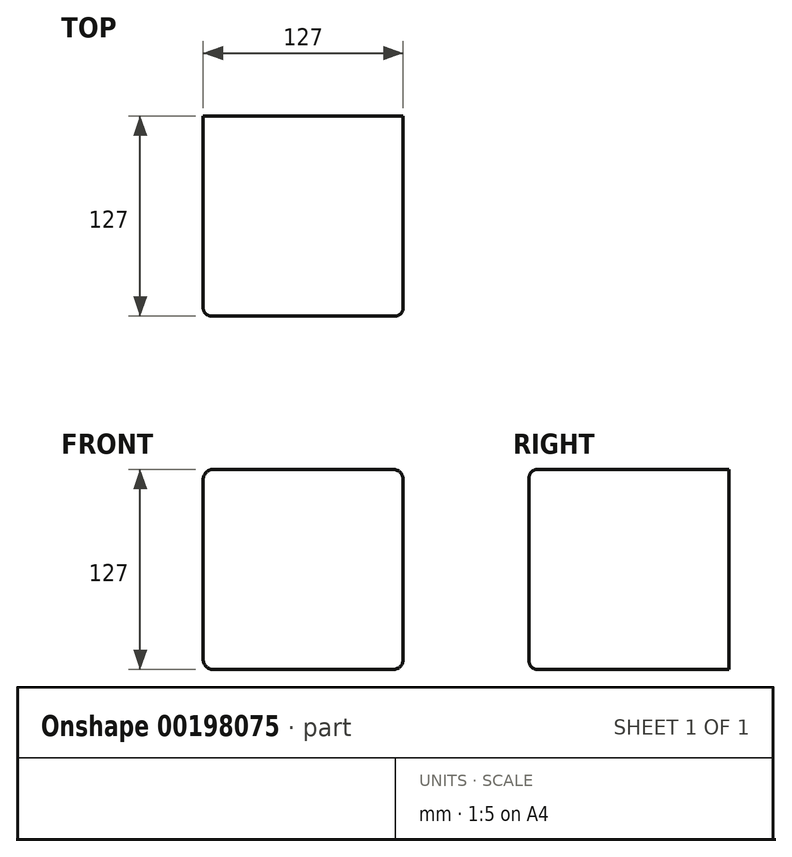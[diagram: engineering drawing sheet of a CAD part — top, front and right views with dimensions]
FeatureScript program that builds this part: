
annotation { "Feature Type Name" : "Feature", "Feature Type Description" : "" }
export const myFeature = defineFeature(function(context is Context, id is Id, definition is map)
    precondition{}
    {
        {
            var Q0;
            Q0=qCreatedBy(makeId("Front.planeOp"),FACE);
            var sketch = newSketch(context, id + "F0", { "sketchPlane" : qUnion([Q0])});
            skLineSegment(sketch, "E0.bottom", {"start": v(57.15, 63.5) * mm, "end": v(-57.15, 63.5) * mm});
            skLineSegment(sketch, "E0.top", {"start": v(57.15, -63.5) * mm, "end": v(-57.15, -63.5) * mm});
            skLineSegment(sketch, "E0.left", {"start": v(63.5, 57.15) * mm, "end": v(63.5, -57.15) * mm});
            skLineSegment(sketch, "E0.right", {"start": v(-63.5, 57.15) * mm, "end": v(-63.5, -57.15) * mm});
            skPoint(sketch, "E0.middle", {"position": v(0, 0) * mm});
            skPoint(sketch, "E1.visualSharp", {"position": v(-63.5, 63.5) * mm});
            skArc(sketch, "E1.filletArc", {"start": v(-57.15, 63.5) * mm, "mid": v(-61.64, 61.64) * mm, "end": v(-63.5, 57.15) * mm});
            skPoint(sketch, "E2.visualSharp", {"position": v(63.5, 63.5) * mm});
            skArc(sketch, "E2.filletArc", {"start": v(63.5, 57.15) * mm, "mid": v(61.64, 61.64) * mm, "end": v(57.15, 63.5) * mm});
            skPoint(sketch, "E3.visualSharp", {"position": v(63.5, -63.5) * mm});
            skArc(sketch, "E3.filletArc", {"start": v(57.15, -63.5) * mm, "mid": v(61.64, -61.64) * mm, "end": v(63.5, -57.15) * mm});
            skPoint(sketch, "E4.visualSharp", {"position": v(-63.5, -63.5) * mm});
            skArc(sketch, "E4.filletArc", {"start": v(-63.5, -57.15) * mm, "mid": v(-61.64, -61.64) * mm, "end": v(-57.15, -63.5) * mm});
            skSolve(sketch);
        }
        {
            var Q0;
            Q0=makeQuery(id+"F0.imprint","IMPRINT",FACE,{"disambiguationData":[TD([[makeQuery(id+"F0.imprint","IMPRINT",EDGE,{"derivedFrom":sQuery(id+"F0.wireOp",EDGE,"E0.bottom")}),1.0]])]});
            extrude(context, id + "F1", {"entities" : qUnion([Q0]), "depth" : 127 * mm});
        }
        {
            var Q0;
            Q0=makeQuery(id+"F1.opExtrude","CAP_EDGE",EDGE,{"disambiguationData":[OSD([sQuery(id+"F0.wireOp",EDGE,"E0.top")])],"isStart":false});
            fillet(context, id + "F2", {"entities" : qUnion([Q0]), "radius" : 5.08 * mm, "tangentPropagation" : true, "allowEdgeOverflow" : false});
        }
    });
